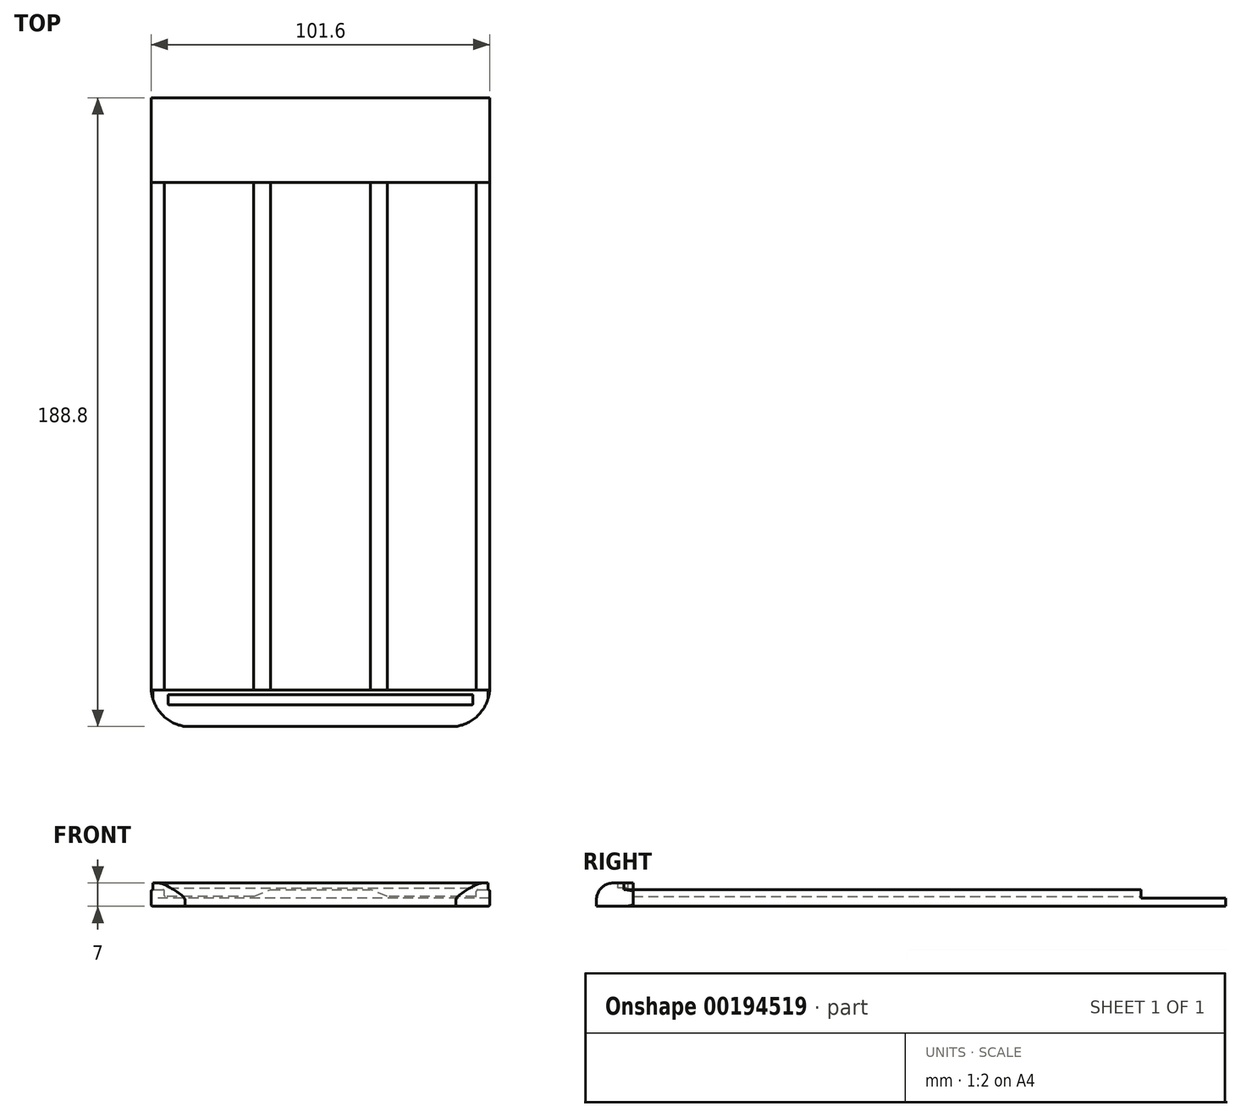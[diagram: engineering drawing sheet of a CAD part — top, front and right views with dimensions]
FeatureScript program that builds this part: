
annotation { "Feature Type Name" : "Feature", "Feature Type Description" : "" }
export const myFeature = defineFeature(function(context is Context, id is Id, definition is map)
    precondition{}
    {
        {
            var Q0;
            Q0=qCreatedBy(makeId("Front.planeOp"),FACE);
            var sketch = newSketch(context, id + "F0", { "sketchPlane" : qUnion([Q0])});
            skLineSegment(sketch, "E0.bottom", {"start": v(0.5, 0) * mm, "end": v(101.1, 0) * mm});
            skLineSegment(sketch, "E0.top", {"start": v(0.5, 5) * mm, "end": v(3.5, 5) * mm});
            skLineSegment(sketch, "E0.left", {"start": v(0, 0.5) * mm, "end": v(0, 4.5) * mm});
            skLineSegment(sketch, "E0.right", {"start": v(101.6, 0.5) * mm, "end": v(101.6, 4.5) * mm});
            skLineSegment(sketch, "E1.top", {"start": v(4.2, 3) * mm, "end": v(30.72, 3) * mm});
            skLineSegment(sketch, "E1.left", {"start": v(4, 4.5) * mm, "end": v(4, 3.2) * mm});
            skLineSegment(sketch, "E1.right", {"start": v(97.6, 4.5) * mm, "end": v(97.6, 3.2) * mm});
            skLineSegment(sketch, "E2.trimOffspring", {"start": v(98.1, 5) * mm, "end": v(101.1, 5) * mm});
            skPoint(sketch, "E3.visualSharp", {"position": v(0, 5) * mm});
            skArc(sketch, "E3.filletArc", {"start": v(0.5, 5) * mm, "mid": v(0.15, 4.85) * mm, "end": v(0, 4.5) * mm});
            skPoint(sketch, "E4.visualSharp", {"position": v(4, 5) * mm});
            skArc(sketch, "E4.filletArc", {"start": v(4, 4.5) * mm, "mid": v(3.85, 4.85) * mm, "end": v(3.5, 5) * mm});
            skPoint(sketch, "E5.visualSharp", {"position": v(4, 3) * mm});
            skArc(sketch, "E5.filletArc", {"start": v(4, 3.2) * mm, "mid": v(4.06, 3.06) * mm, "end": v(4.2, 3) * mm});
            skPoint(sketch, "E6.visualSharp", {"position": v(97.6, 3) * mm});
            skArc(sketch, "E6.filletArc", {"start": v(97.4, 3) * mm, "mid": v(97.54, 3.06) * mm, "end": v(97.6, 3.2) * mm});
            skPoint(sketch, "E7.visualSharp", {"position": v(97.6, 5) * mm});
            skArc(sketch, "E7.filletArc", {"start": v(98.1, 5) * mm, "mid": v(97.75, 4.85) * mm, "end": v(97.6, 4.5) * mm});
            skPoint(sketch, "E8.visualSharp", {"position": v(101.6, 5) * mm});
            skArc(sketch, "E8.filletArc", {"start": v(101.6, 4.5) * mm, "mid": v(101.45, 4.85) * mm, "end": v(101.1, 5) * mm});
            skPoint(sketch, "E9.visualSharp", {"position": v(101.6, 0) * mm});
            skArc(sketch, "E9.filletArc", {"start": v(101.1, 0) * mm, "mid": v(101.45, 0.15) * mm, "end": v(101.6, 0.5) * mm});
            skPoint(sketch, "E10.visualSharp", {"position": v(0, 0) * mm});
            skArc(sketch, "E10.filletArc", {"start": v(0, 0.5) * mm, "mid": v(0.15, 0.15) * mm, "end": v(0.5, 0) * mm});
            skLineSegment(sketch, "E11", {"start": v(35.8, 5) * mm, "end": v(65.8, 5) * mm});
            skLineSegment(sketch, "E12", {"start": v(65.8, 5) * mm, "end": v(70.88, 3) * mm});
            skLineSegment(sketch, "E13", {"start": v(35.8, 5) * mm, "end": v(30.72, 3) * mm});
            skLineSegment(sketch, "E14", {"start": v(50.8, 5) * mm, "end": v(50.8, 0) * mm, "construction": true});
            skLineSegment(sketch, "E15.trimOffspring", {"start": v(70.88, 3) * mm, "end": v(97.4, 3) * mm});
            skSolve(sketch);
        }
        {
            var Q0;
            Q0 = qSketchRegion(id + "F0", true);
            extrude(context, id + "F1", {"entities" : qUnion([Q0]), "depth" : 177.8 * mm});
        }
        {
            var Q0;
            Q0=makeQuery(id+"F1.opExtrude","CAP_FACE",FACE,{"disambiguationData":[OSD([sQuery(id+"F0.wireOp",EDGE,"E0.bottom"),sQuery(id+"F0.wireOp",EDGE,"E0.top"),sQuery(id+"F0.wireOp",EDGE,"E0.left"),sQuery(id+"F0.wireOp",EDGE,"E0.right"),sQuery(id+"F0.wireOp",EDGE,"E1.top"),sQuery(id+"F0.wireOp",EDGE,"E1.left"),sQuery(id+"F0.wireOp",EDGE,"E1.right"),sQuery(id+"F0.wireOp",EDGE,"E2.trimOffspring"),sQuery(id+"F0.wireOp",EDGE,"E3.filletArc"),sQuery(id+"F0.wireOp",EDGE,"E4.filletArc"),sQuery(id+"F0.wireOp",EDGE,"E5.filletArc"),sQuery(id+"F0.wireOp",EDGE,"E6.filletArc"),sQuery(id+"F0.wireOp",EDGE,"E7.filletArc"),sQuery(id+"F0.wireOp",EDGE,"E8.filletArc"),sQuery(id+"F0.wireOp",EDGE,"E9.filletArc"),sQuery(id+"F0.wireOp",EDGE,"E10.filletArc"),sQuery(id+"F0.wireOp",EDGE,"E11"),sQuery(id+"F0.wireOp",EDGE,"E12"),sQuery(id+"F0.wireOp",EDGE,"E13"),sQuery(id+"F0.wireOp",EDGE,"E15.trimOffspring")])],"isStart":true});
            var sketch = newSketch(context, id + "F2", { "sketchPlane" : qUnion([Q0])});
            skLineSegment(sketch, "E16.bottom", {"start": v(-101.6, 5) * mm, "end": v(0, 5) * mm});
            skLineSegment(sketch, "E16.top", {"start": v(-101.6, 2.5) * mm, "end": v(0, 2.5) * mm});
            skLineSegment(sketch, "E16.left", {"start": v(-101.6, 5) * mm, "end": v(-101.6, 2.5) * mm});
            skLineSegment(sketch, "E16.right", {"start": v(0, 5) * mm, "end": v(0, 2.5) * mm});
            skSolve(sketch);
        }
        {
            var Q0;
            Q0 = qSketchRegion(id + "F2", true);
            extrude(context, id + "F3", {"entities" : qUnion([Q0]), "operationType" : NewBodyOperationType.REMOVE, "oppositeDirection" : true, "depth" : 25.4 * mm});
        }
        {
            var Q0;
            Q0=makeQuery(id+"F1.opExtrude","CAP_FACE",FACE,{"disambiguationData":[OSD([sQuery(id+"F0.wireOp",EDGE,"E0.bottom"),sQuery(id+"F0.wireOp",EDGE,"E0.top"),sQuery(id+"F0.wireOp",EDGE,"E0.left"),sQuery(id+"F0.wireOp",EDGE,"E0.right"),sQuery(id+"F0.wireOp",EDGE,"E1.top"),sQuery(id+"F0.wireOp",EDGE,"E1.left"),sQuery(id+"F0.wireOp",EDGE,"E1.right"),sQuery(id+"F0.wireOp",EDGE,"E2.trimOffspring"),sQuery(id+"F0.wireOp",EDGE,"E3.filletArc"),sQuery(id+"F0.wireOp",EDGE,"E4.filletArc"),sQuery(id+"F0.wireOp",EDGE,"E5.filletArc"),sQuery(id+"F0.wireOp",EDGE,"E6.filletArc"),sQuery(id+"F0.wireOp",EDGE,"E7.filletArc"),sQuery(id+"F0.wireOp",EDGE,"E8.filletArc"),sQuery(id+"F0.wireOp",EDGE,"E9.filletArc"),sQuery(id+"F0.wireOp",EDGE,"E10.filletArc"),sQuery(id+"F0.wireOp",EDGE,"E11"),sQuery(id+"F0.wireOp",EDGE,"E12"),sQuery(id+"F0.wireOp",EDGE,"E13"),sQuery(id+"F0.wireOp",EDGE,"E15.trimOffspring")])],"isStart":false});
            var sketch = newSketch(context, id + "F4", { "sketchPlane" : qUnion([Q0])});
            skLineSegment(sketch, "E17.bottom", {"start": v(0.5, 0) * mm, "end": v(101.1, 0) * mm});
            skLineSegment(sketch, "E17.top", {"start": v(0.5, 5) * mm, "end": v(101.1, 5) * mm});
            skLineSegment(sketch, "E17.left", {"start": v(0, 0.5) * mm, "end": v(0, 4.5) * mm});
            skLineSegment(sketch, "E17.right", {"start": v(101.6, 0.5) * mm, "end": v(101.6, 4.5) * mm});
            skPoint(sketch, "E18.visualSharp", {"position": v(101.6, 5) * mm});
            skArc(sketch, "E18.filletArc", {"start": v(101.6, 4.5) * mm, "mid": v(101.45, 4.85) * mm, "end": v(101.1, 5) * mm});
            skPoint(sketch, "E19.visualSharp", {"position": v(101.6, 0) * mm});
            skArc(sketch, "E19.filletArc", {"start": v(101.1, 0) * mm, "mid": v(101.45, 0.15) * mm, "end": v(101.6, 0.5) * mm});
            skPoint(sketch, "E20.visualSharp", {"position": v(0, 5) * mm});
            skArc(sketch, "E20.filletArc", {"start": v(0.5, 5) * mm, "mid": v(0.15, 4.85) * mm, "end": v(0, 4.5) * mm});
            skPoint(sketch, "E21.visualSharp", {"position": v(0, 0) * mm});
            skArc(sketch, "E21.filletArc", {"start": v(0, 0.5) * mm, "mid": v(0.15, 0.15) * mm, "end": v(0.5, 0) * mm});
            skSolve(sketch);
        }
        {
            var Q0;
            Q0 = qSketchRegion(id + "F4", true);
            extrude(context, id + "F5", {"entities" : qUnion([Q0]), "operationType" : NewBodyOperationType.ADD, "depth" : 11 * mm});
        }
        {
            var Q0;
            Q0=makeQuery(id+"F5.boolean.opBoolean","MERGE",FACE,{"derivedFrom":[makeQuery(id+"F1.opExtrude","SWEPT_FACE",FACE,{"disambiguationData":[OSD([sQuery(id+"F0.wireOp",EDGE,"E0.top")])]}),makeQuery(id+"F1.opExtrude","SWEPT_FACE",FACE,{"disambiguationData":[OSD([sQuery(id+"F0.wireOp",EDGE,"E2.trimOffspring")])]}),makeQuery(id+"F1.opExtrude","SWEPT_FACE",FACE,{"disambiguationData":[OSD([sQuery(id+"F0.wireOp",EDGE,"E11")])]}),makeQuery(id+"F5.opExtrude","SWEPT_FACE",FACE,{"disambiguationData":[OSD([sQuery(id+"F4.wireOp",EDGE,"E17.top")])]})]});
            var sketch = newSketch(context, id + "F6", { "sketchPlane" : qUnion([Q0])});
            skLineSegment(sketch, "E22.bottom", {"start": v(0.5, -177.8) * mm, "end": v(101.1, -177.8) * mm});
            skLineSegment(sketch, "E22.top", {"start": v(0.5, -188.8) * mm, "end": v(101.1, -188.8) * mm});
            skLineSegment(sketch, "E22.left", {"start": v(0.5, -177.8) * mm, "end": v(0.5, -188.8) * mm});
            skLineSegment(sketch, "E22.right", {"start": v(101.1, -177.8) * mm, "end": v(101.1, -188.8) * mm});
            skSolve(sketch);
        }
        {
            var Q0;
            Q0 = qSketchRegion(id + "F6", true);
            extrude(context, id + "F7", {"entities" : qUnion([Q0]), "operationType" : NewBodyOperationType.ADD, "depth" : 2 * mm});
        }
        {
            var Q0;
            Q0=makeQuery(id+"F7.opExtrude","CAP_FACE",FACE,{"disambiguationData":[OSD([sQuery(id+"F6.wireOp",EDGE,"E22.bottom"),sQuery(id+"F6.wireOp",EDGE,"E22.top"),sQuery(id+"F6.wireOp",EDGE,"E22.left"),sQuery(id+"F6.wireOp",EDGE,"E22.right")])],"isStart":false});
            var sketch = newSketch(context, id + "F8", { "sketchPlane" : qUnion([Q0])});
            skArc(sketch, "E23", {"start": v(0, -177.8) * mm, "mid": v(3.14, -185.1) * mm, "end": v(10.16, -188.8) * mm});
            skLineSegment(sketch, "E24", {"start": v(0, -177.8) * mm, "end": v(0, -188.8) * mm});
            skLineSegment(sketch, "E25", {"start": v(10.16, -188.8) * mm, "end": v(0, -188.8) * mm});
            skLineSegment(sketch, "E26", {"start": v(50.8, -188.8) * mm, "end": v(50.8, -177.8) * mm, "construction": true});
            skArc(sketch, "E27.MirrorCS", {"start": v(101.6, -177.8) * mm, "mid": v(98.46, -185.1) * mm, "end": v(91.44, -188.8) * mm});
            skLineSegment(sketch, "E28.MirrorCS", {"start": v(101.6, -177.8) * mm, "end": v(101.6, -188.8) * mm});
            skLineSegment(sketch, "E29.MirrorCS", {"start": v(91.44, -188.8) * mm, "end": v(101.6, -188.8) * mm});
            skSolve(sketch);
        }
        {
            var Q0;
            {var subQ1=sQuery(id+"F8.wireOp",EDGE,"E23");var subQ3=makeQuery(id+"F7.opExtrude","CAP_EDGE",EDGE,{"disambiguationData":[OSD([sQuery(id+"F6.wireOp",EDGE,"E22.left")])],"isStart":false});var subQ4=makeQuery(id+"F8.imprint","INTERSECT",VERTEX,{"derivedFrom":[subQ3,subQ1]});Q0=makeQuery(id+"F8.imprint","IMPRINT",FACE,{"disambiguationData":[TD([[makeQuery(id+"F8.imprint","IMPRINT",EDGE,{"disambiguationData":[TD([[subQ4,1.0]])],"derivedFrom":subQ3}),-1.0]])]});}
            var Q1;
            {var subQ0=sQuery(id+"F8.wireOp",EDGE,"E24");Q1=makeQuery(id+"F8.imprint","IMPRINT",FACE,{"disambiguationData":[TD([[makeQuery(id+"F8.imprint","IMPRINT",EDGE,{"derivedFrom":subQ0}),1.0]])]});}
            var Q2;
            {var subQ1=sQuery(id+"F8.wireOp",EDGE,"E27.MirrorCS");var subQ3=makeQuery(id+"F7.opExtrude","CAP_EDGE",EDGE,{"disambiguationData":[OSD([sQuery(id+"F6.wireOp",EDGE,"E22.right")])],"isStart":false});var subQ4=makeQuery(id+"F8.imprint","INTERSECT",VERTEX,{"derivedFrom":[subQ3,subQ1]});Q2=makeQuery(id+"F8.imprint","IMPRINT",FACE,{"disambiguationData":[TD([[makeQuery(id+"F8.imprint","IMPRINT",EDGE,{"disambiguationData":[TD([[subQ4,1.0]])],"derivedFrom":subQ3}),1.0]])]});}
            var Q3;
            {var subQ0=sQuery(id+"F8.wireOp",EDGE,"E28.MirrorCS");Q3=makeQuery(id+"F8.imprint","IMPRINT",FACE,{"disambiguationData":[TD([[makeQuery(id+"F8.imprint","IMPRINT",EDGE,{"derivedFrom":subQ0}),-1.0]])]});}
            extrude(context, id + "F9", {"entities" : qUnion([Q0, Q1, Q2, Q3]), "operationType" : NewBodyOperationType.REMOVE, "oppositeDirection" : true, "depth" : 25.4 * mm});
        }
        {
            var Q0;
            Q0=makeQuery(id+"F7.opExtrude","CAP_EDGE",EDGE,{"disambiguationData":[OSD([sQuery(id+"F6.wireOp",EDGE,"E22.top")])],"isStart":false});
            fillet(context, id + "F10", {"entities" : qUnion([Q0]), "radius" : 5.08 * mm, "tangentPropagation" : true, "allowEdgeOverflow" : false});
        }
        {
            var Q0;
            Q0=makeQuery(id+"F7.opExtrude","CAP_FACE",FACE,{"disambiguationData":[OSD([sQuery(id+"F6.wireOp",EDGE,"E22.bottom"),sQuery(id+"F6.wireOp",EDGE,"E22.top"),sQuery(id+"F6.wireOp",EDGE,"E22.left"),sQuery(id+"F6.wireOp",EDGE,"E22.right")])],"isStart":false});
            var sketch = newSketch(context, id + "F11", { "sketchPlane" : qUnion([Q0])});
            skLineSegment(sketch, "E30.bottom", {"start": v(5.28, -179.24) * mm, "end": v(96.32, -179.24) * mm});
            skLineSegment(sketch, "E30.top", {"start": v(5.28, -182.28) * mm, "end": v(96.32, -182.28) * mm});
            skLineSegment(sketch, "E30.left", {"start": v(5.08, -179.44) * mm, "end": v(5.08, -182.08) * mm});
            skLineSegment(sketch, "E30.right", {"start": v(96.52, -179.44) * mm, "end": v(96.52, -182.08) * mm});
            skLineSegment(sketch, "E31", {"start": v(50.8, -177.8) * mm, "end": v(50.8, -183.72) * mm, "construction": true});
            skLineSegment(sketch, "E32", {"start": v(50.8, -180.76) * mm, "end": v(38.95, -180.76) * mm, "construction": true});
            skPoint(sketch, "E33.visualSharp", {"position": v(5.08, -179.24) * mm});
            skArc(sketch, "E33.filletArc", {"start": v(5.28, -179.24) * mm, "mid": v(5.14, -179.3) * mm, "end": v(5.08, -179.44) * mm});
            skPoint(sketch, "E34.visualSharp", {"position": v(5.08, -182.28) * mm});
            skArc(sketch, "E34.filletArc", {"start": v(5.08, -182.08) * mm, "mid": v(5.14, -182.23) * mm, "end": v(5.28, -182.28) * mm});
            skPoint(sketch, "E35.visualSharp", {"position": v(96.52, -179.24) * mm});
            skArc(sketch, "E35.filletArc", {"start": v(96.52, -179.44) * mm, "mid": v(96.46, -179.3) * mm, "end": v(96.32, -179.24) * mm});
            skPoint(sketch, "E36.visualSharp", {"position": v(96.52, -182.28) * mm});
            skArc(sketch, "E36.filletArc", {"start": v(96.32, -182.28) * mm, "mid": v(96.46, -182.23) * mm, "end": v(96.52, -182.08) * mm});
            skSolve(sketch);
        }
        {
            var Q0;
            Q0=makeQuery(id+"F11.imprint","IMPRINT",FACE,{"disambiguationData":[TD([[makeQuery(id+"F11.imprint","IMPRINT",EDGE,{"derivedFrom":sQuery(id+"F11.wireOp",EDGE,"E30.bottom")}),-1.0]])]});
            extrude(context, id + "F12", {"entities" : qUnion([Q0]), "operationType" : NewBodyOperationType.REMOVE, "oppositeDirection" : true, "depth" : 1.5 * mm});
        }
    });
